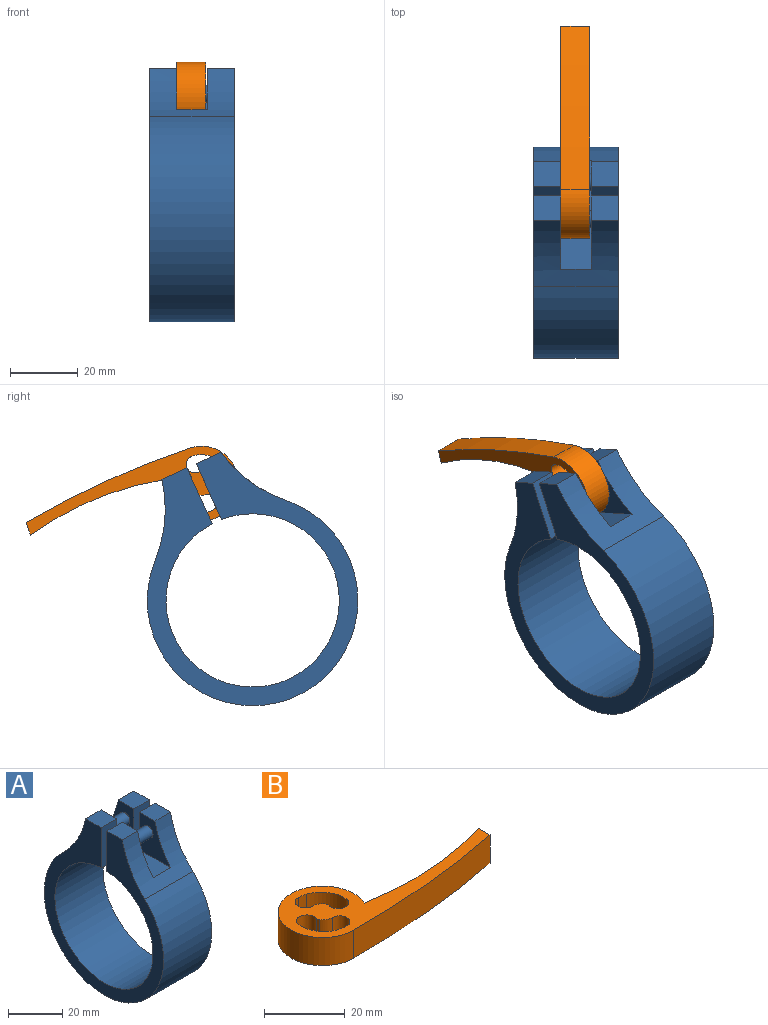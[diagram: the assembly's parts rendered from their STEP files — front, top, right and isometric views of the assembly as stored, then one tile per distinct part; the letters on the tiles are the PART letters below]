
ASSEMBLY  parts=2 mates=1
PART A: 20 faces, bbox 25x62x74.5 mm
  f0: plane 8.05x8mm, normal (0,0,1), area 64.4mm2, adj f3,f6,f12,f17
  f1: plane 8.05x8mm, normal (0,0,1), area 64.4mm2, adj f4,f6,f11,f17
  f2: plane 16.11x9mm, normal (0,0,1), area 145mm2, adj f3,f4,f6,f17
  f3: plane 16.96x16.11mm, normal (1,0,0), area 171.2mm2, adj f0,f2,f6,f17,f19
  f4: plane 16.96x16.11mm, normal (-1,0,0), area 171.2mm2, adj f1,f2,f6,f17,f19
  f5: cylinder r=40mm len=25mm, axis (-1,0,0), area 438.6mm2, adj f7,f8,f9,f11,f12,f13,f14,f15
  f6: cylinder r=40mm len=25mm, axis (-1,0,0), area 438.6mm2, adj f0,f1,f2,f3,f4,f9,f11,f12
  f7: plane 8x7.95mm, normal (0,0,1), area 63.6mm2, adj f5,f12,f14,f16
  f8: plane 8x7.95mm, normal (0,0,1), area 63.6mm2, adj f5,f11,f15,f16
  f9: cylinder r=31mm len=62mm, axis (-1,0,0), area 3699.5mm2, adj f5,f6,f11,f12
  f10: cylinder r=25.5mm len=51mm, axis (-1,0,0), area 3930.5mm2, adj f11,f12,f16,f17
  f11: plane 74.5x62mm, normal (1,0,0), area 1260.3mm2, adj f1,f5,f6,f8,f9,f10,f16,f17
  f12: plane 74.5x62mm, normal (-1,0,0), area 1260.3mm2, adj f0,f5,f6,f7,f9,f10,f16,f17
  f13: plane 16.01x9mm, normal (0,0,1), area 144.1mm2, adj f5,f14,f15,f16
  f14: plane 16.96x16.01mm, normal (1,0,0), area 169.5mm2, adj f5,f7,f13,f16,f18
  f15: plane 16.96x16.01mm, normal (-1,0,0), area 169.5mm2, adj f5,f8,f13,f16,f18
  f16: plane 25x18.05mm, normal (0,1,0), area 298.6mm2, adj f7,f8,f10,f11,f12,f13,f14,f15
  f17: plane 25x18.04mm, normal (0,-1,0), area 298.4mm2, adj f0,f1,f2,f3,f4,f10,f11,f12
  f18: cylinder r=2.5mm len=9mm, axis (1,0,0), area 141.4mm2, adj f14,f15
  f19: cylinder r=2.5mm len=9mm, axis (1,0,0), area 141.4mm2, adj f3,f4
PART B: 18 faces, bbox 63.5x22x8.5 mm
  f0: cylinder r=2.55mm len=8.5mm, axis (0,0,-1), area 68.1mm2, adj f1,f15,f16,f17
  f1: cylinder r=8.55mm len=8.5mm, axis (0,0,-1), area 21.3mm2, adj f0,f2,f16,f17
  f2: cylinder r=8.07mm len=8.5mm, axis (0,0,-1), area 92.9mm2, adj f1,f3,f16,f17
  f3: cylinder r=2.55mm len=8.5mm, axis (0,0,-1), area 74.5mm2, adj f2,f4,f16,f17
  f4: cylinder r=3.18mm len=8.5mm, axis (0,0,-1), area 9.4mm2, adj f3,f15,f16,f17
  f5: cylinder r=8.07mm len=8.5mm, axis (0,0,-1), area 92.9mm2, adj f6,f13,f16,f17
  f6: cylinder r=2.55mm len=8.5mm, axis (0,0,-1), area 74.7mm2, adj f5,f7,f16,f17
  f7: cylinder r=3.2mm len=8.5mm, axis (0,0,-1), area 8.1mm2, adj f6,f8,f16,f17
  f8: cylinder r=3.45mm len=8.5mm, axis (0,0,-1), area 28.8mm2, adj f7,f9,f16,f17
  f9: cylinder r=2.55mm len=8.5mm, axis (0,0,-1), area 68.1mm2, adj f8,f13,f16,f17
  f10: cylinder r=265.3mm len=52.56mm, axis (0,0,-1), area 449.5mm2, adj f11,f14,f16,f17
  f11: plane 8.5x3.97mm, normal (1,0,0), area 33.8mm2, adj f10,f12,f16,f17
  f12: cylinder r=92.02mm len=42.55mm, axis (0,0,-1), area 365.7mm2, adj f11,f14,f16,f17
  f13: cylinder r=8.55mm len=8.5mm, axis (0,0,-1), area 21.3mm2, adj f5,f9,f16,f17
  f14: cylinder r=11mm len=22mm, axis (0,0,-1), area 481.2mm2, adj f10,f12,f16,f17
  f15: cylinder r=3.45mm len=8.5mm, axis (0,0,-1), area 27.7mm2, adj f0,f4,f16,f17
  f16: plane 63.51x22mm, normal (0,0,1), area 433.5mm2, adj f0,f1,f2,f3,f4,f5,f6,f7
  f17: plane 63.51x22mm, normal (0,0,-1), area 433.5mm2, adj f0,f1,f2,f3,f4,f5,f6,f7
PLACE A rot(axis=(-1,0,0),24.5deg) t=(0.32,-41.47,37.83)mm fixed
PLACE B rot(axis=(-0.63,-0.45,0.63),131.5deg) t=(16.82,-26.82,71.28)mm
MATE revolute B.f6 <-> A.f18  axis (-1,0,0) through (8.32,-32.02,73.07)mm
